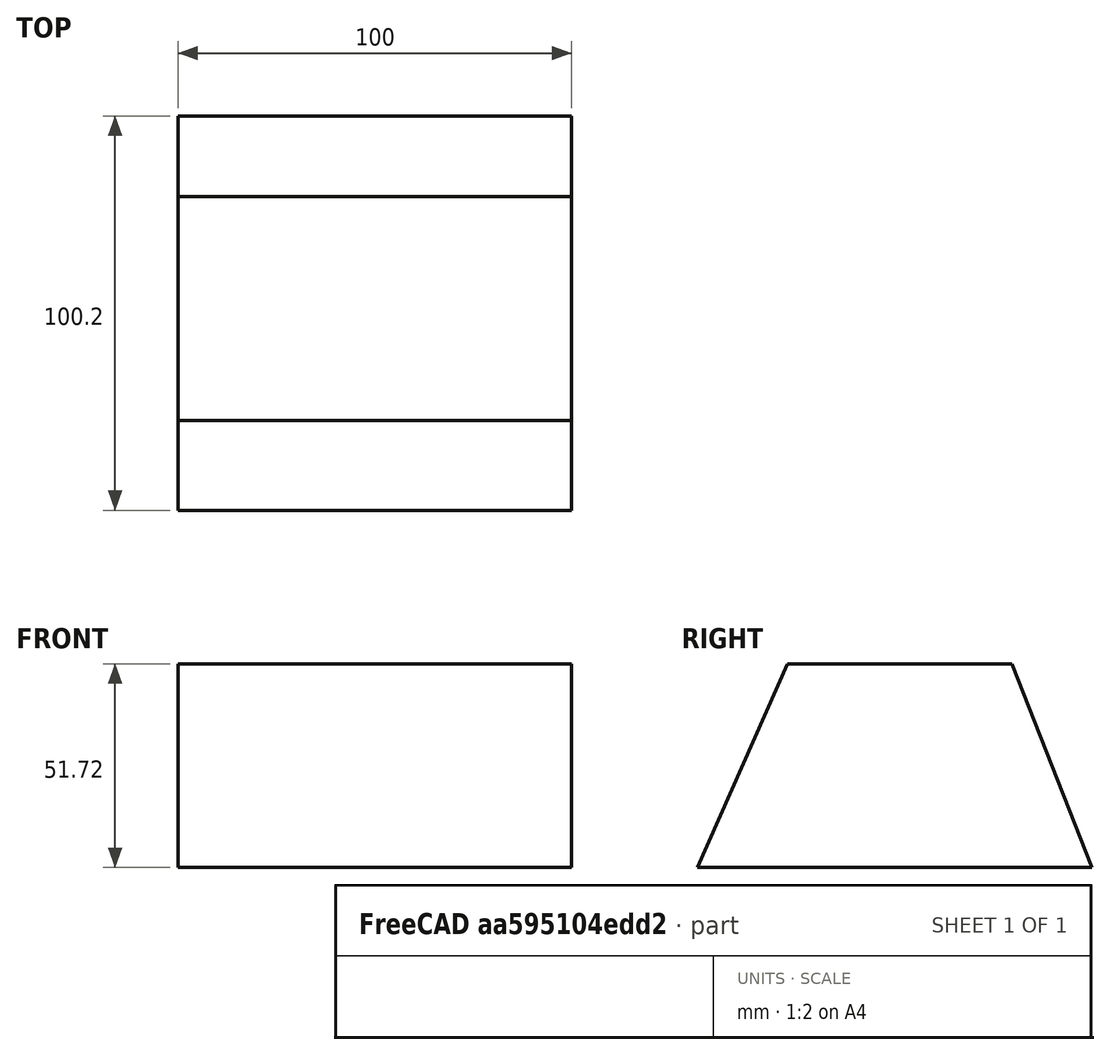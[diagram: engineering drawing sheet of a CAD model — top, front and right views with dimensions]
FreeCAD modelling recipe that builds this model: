
FCSTD DOCUMENT  (FreeCAD 0.21R33694 (Git))
Label: OJT1_T16R01_lingot
License: All rights reserved
LicenseURL: https://en.wikipedia.org/wiki/All_rights_reserved
objects: Sketcher::SketchObject×1, PartDesign::Pad×1, PartDesign::Body×1
note: 4 computed .brp shape members not serialized (recipe doc carries the construction recipe); baked Part::Feature solids carry a one-line shape summary decoded from their .brp

FEATURE [Sketcher::SketchObject] Sketch  label="lingot-or"
  AttachmentOffset = pos=(2,0,0) rot=(0,0,1;0rad)
  FullyConstrained = false
  MapMode = 5
  Placement = pos=(4e-16,2,-4e-16) rot=(0.57735,0.57735,0.57735;2.0944rad)
  Support = -> [YZ_Plane]
  sketch-geometry (4):
    g0: LineSegment StartX=-30.505 StartY=24.5455 StartZ=0 EndX=-53.3333 EndY=-27.1717 EndZ=0
    g1: LineSegment StartX=-53.3333 StartY=-27.1717 StartZ=0 EndX=46.8687 EndY=-27.1717 EndZ=0
    g2: LineSegment StartX=46.8687 StartY=-27.1717 StartZ=0 EndX=26.4646 EndY=24.5455 EndZ=0
    g3: LineSegment StartX=26.4646 StartY=24.5455 StartZ=0 EndX=-30.505 EndY=24.5455 EndZ=0
  constraints (6):
    c: Coincident(g0,g1)
    c: Horizontal(g1)
    c: Coincident(g1,g2)
    c: Coincident(g2,g3)
    c: Coincident(g3,g0)
    c: Horizontal(g3)
FEATURE [PartDesign::Pad] Pad  label="LINGOT D'OR"
  Direction = (1,-2e-16,3e-16)
  Length = 100
  Length2 = 10
  Placement = pos=(0,0,0) rot=(1,1,1;2.0944rad)
  Profile = -> Sketch
  ReferenceAxis = -> Sketch [N_Axis]
  Type = 0
FEATURE [PartDesign::Body] Body
  Group = -> [Sketch,Pad]
  Origin = -> Origin
  Tip = -> Pad
